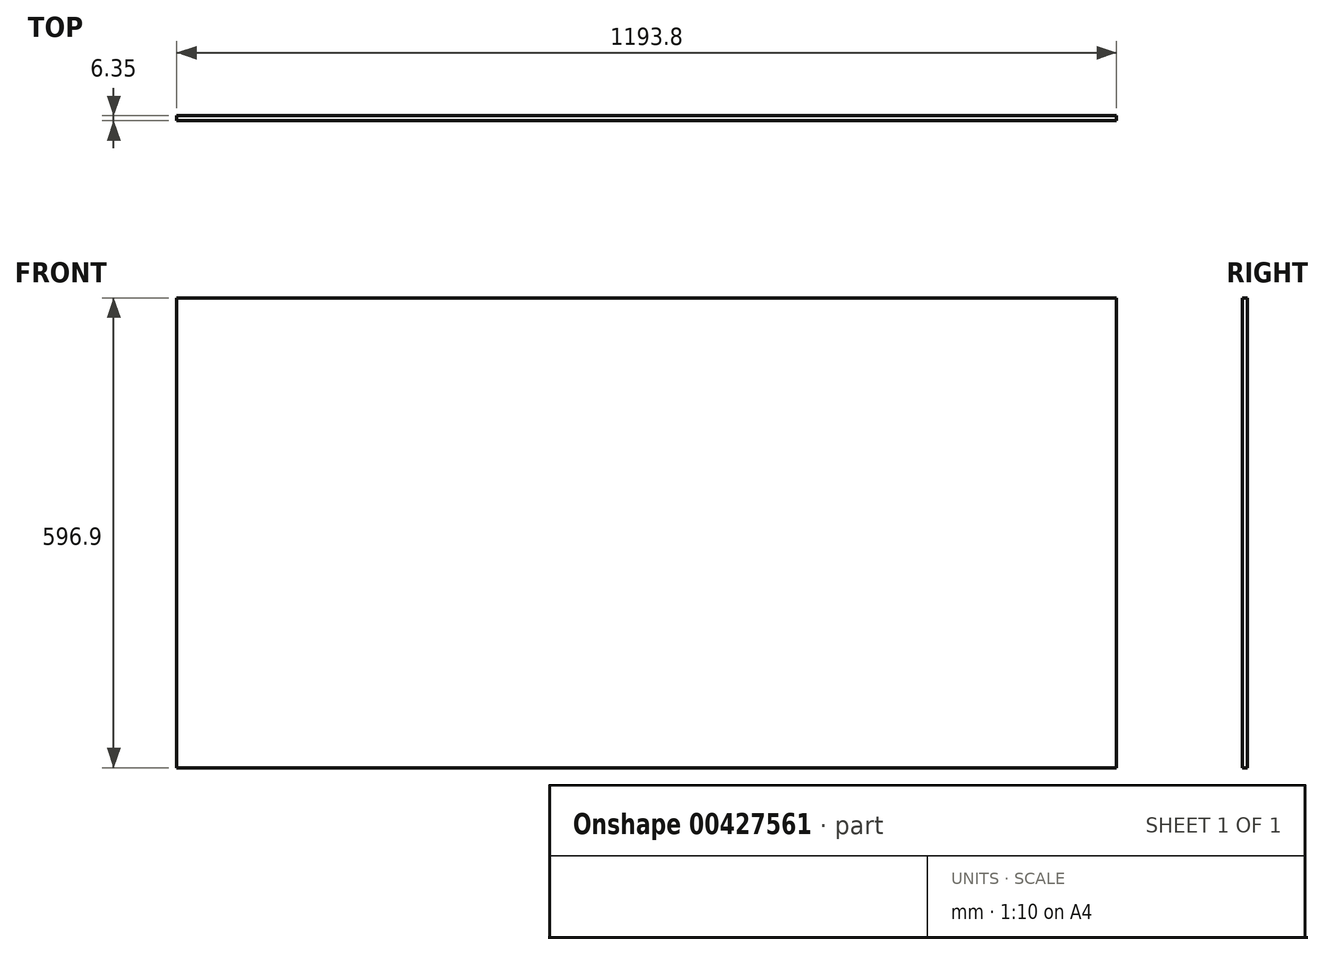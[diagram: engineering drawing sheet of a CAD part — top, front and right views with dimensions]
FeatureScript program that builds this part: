
annotation { "Feature Type Name" : "Feature", "Feature Type Description" : "" }
export const myFeature = defineFeature(function(context is Context, id is Id, definition is map)
    precondition{}
    {
        {
            var Q0;
            Q0=qCreatedBy(makeId("Front.planeOp"),FACE);
            var sketch = newSketch(context, id + "F0", { "sketchPlane" : qUnion([Q0])});
            skLineSegment(sketch, "E0.bottom", {"start": v(0, 0) * mm, "end": v(1193.8, 0) * mm});
            skLineSegment(sketch, "E0.top", {"start": v(0, 596.9) * mm, "end": v(1193.8, 596.9) * mm});
            skLineSegment(sketch, "E0.left", {"start": v(0, 0) * mm, "end": v(0, 596.9) * mm});
            skLineSegment(sketch, "E0.right", {"start": v(1193.8, 0) * mm, "end": v(1193.8, 596.9) * mm});
            skSolve(sketch);
        }
        {
            var Q0;
            Q0 = qSketchRegion(id + "F0", true);
            extrude(context, id + "F1", {"entities" : qUnion([Q0]), "depth" : 6.35 * mm});
        }
    });
